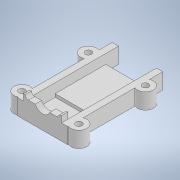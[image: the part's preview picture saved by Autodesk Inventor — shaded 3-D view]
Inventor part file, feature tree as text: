
AUTODESK INVENTOR PART (.ipt)
format: ipt  version: 2020.4 (Build 244396000, 396)  size: 211,968 bytes
history: native  units: mm
features: extrude x7, sketch x7, projected_geometry x1
ambient origin geometry x8: Origin, YZ Plane, XZ Plane, XY Plane, X Axis, Y Axis, Z Axis, Center Point
bodies: Solid1 (feature_tree)
feature tree (15):
  extrude  "Extrusion1"  Depth=30.0mm
  extrude  "Extrusion2"  Depth=2.0mm
  extrude  "Extrusion3"  Depth=2.0mm
  extrude  "Extrusion4"  Depth=5.0mm
  extrude  "Extrusion7"  Depth=5.0mm
  extrude  "Extrusion8"  Depth=2.0mm
  extrude  "Extrusion9"  Depth=10.0mm TaperAngle=0.0deg
  sketch  "Sketch1"  dims[d0=16.0mm d1=30.0mm]
  sketch  "Sketch2"  dims[d2=2.0mm d3=0.0mm d4=2.0mm]
  sketch  "Sketch3"  dims[d5=2.0mm d6=2.0mm]
  projected_geometry  "Projected Loop1"
  sketch  "Sketch4"  dims[d7=3.0mm d8=0.0mm d9=5.0mm]
  sketch  "Sketch8"  dims[d10=5.0mm d11=9.0mm]
  sketch  "Sketch9"  dims[d12=2.0mm d13=2.0mm]
  sketch  "Sketch10"  dims[d14=2.0mm d15=0.0mm d16=10.0mm d17=0.0mm d28=24.0mm d29=10.0mm d30=0.0mm d31=1.0mm d32=7.0mm d33=1.0mm d34=0.0mm d35=2.0mm d36=1.5mm d38=16.0mm d39=20.0mm d41=21.0mm d42=20.0mm d44=18.0mm d47=10.0mm d48=0.0mm d49=26.0mm]
